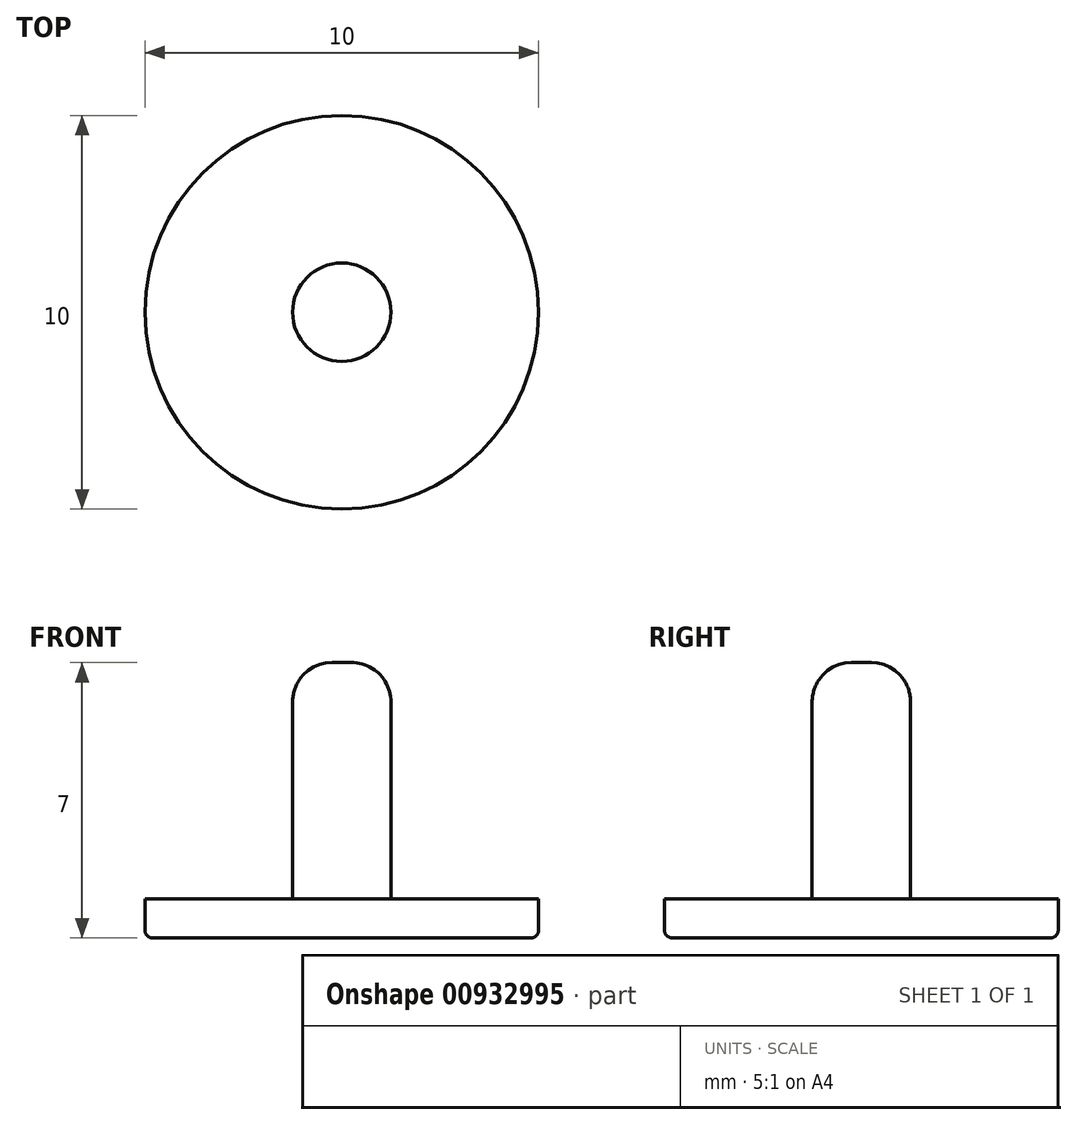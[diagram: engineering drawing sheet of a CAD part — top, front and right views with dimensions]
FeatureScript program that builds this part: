
annotation { "Feature Type Name" : "Feature", "Feature Type Description" : "" }
export const myFeature = defineFeature(function(context is Context, id is Id, definition is map)
    precondition{}
    {
        {
            var Q0;
            Q0=qCreatedBy(makeId("Top.planeOp"),FACE);
            var sketch = newSketch(context, id + "F0", { "sketchPlane" : qUnion([Q0])});
            skCircle(sketch, "E0", {"center": v(0, 0) * mm, "radius": 5 * mm});
            skSolve(sketch);
        }
        {
            var Q0;
            Q0=makeQuery(id+"F0.imprint","IMPRINT",FACE,{"disambiguationData":[TD([[makeQuery(id+"F0.imprint","IMPRINT",EDGE,{"derivedFrom":sQuery(id+"F0.wireOp",EDGE,"E0")}),1.0]])]});
            extrude(context, id + "F1", {"entities" : qUnion([Q0]), "depth" : 1 * mm, "offsetDistance" : 25 * mm});
        }
        {
            var Q0;
            Q0=makeQuery(id+"F1.opExtrude","CAP_FACE",FACE,{"disambiguationData":[OSD([sQuery(id+"F0.wireOp",EDGE,"E0")])],"isStart":false});
            var sketch = newSketch(context, id + "F2", { "sketchPlane" : qUnion([Q0])});
            skCircle(sketch, "E1", {"center": v(0, 0) * mm, "radius": 1.25 * mm});
            skSolve(sketch);
        }
        {
            var Q0;
            Q0=makeQuery(id+"F2.imprint","IMPRINT",FACE,{"disambiguationData":[TD([[makeQuery(id+"F2.imprint","IMPRINT",EDGE,{"derivedFrom":sQuery(id+"F2.wireOp",EDGE,"E1")}),1.0]])]});
            extrude(context, id + "F3", {"entities" : qUnion([Q0]), "operationType" : NewBodyOperationType.ADD, "depth" : 6 * mm, "offsetDistance" : 25 * mm});
        }
        {
            var Q0;
            Q0=makeQuery(id+"F3.opExtrude","CAP_EDGE",EDGE,{"disambiguationData":[OSD([sQuery(id+"F2.wireOp",EDGE,"E1")])],"isStart":false});
            fillet(context, id + "F4", {"entities" : qUnion([Q0]), "radius" : 1 * mm, "tangentPropagation" : true, "allowEdgeOverflow" : false});
        }
        {
            var Q0;
            Q0=makeQuery(id+"F1.opExtrude","CAP_EDGE",EDGE,{"disambiguationData":[OSD([sQuery(id+"F0.wireOp",EDGE,"E0")])],"isStart":true});
            fillet(context, id + "F5", {"entities" : qUnion([Q0]), "radius" : .2 * mm, "tangentPropagation" : true, "allowEdgeOverflow" : false});
        }
    });
